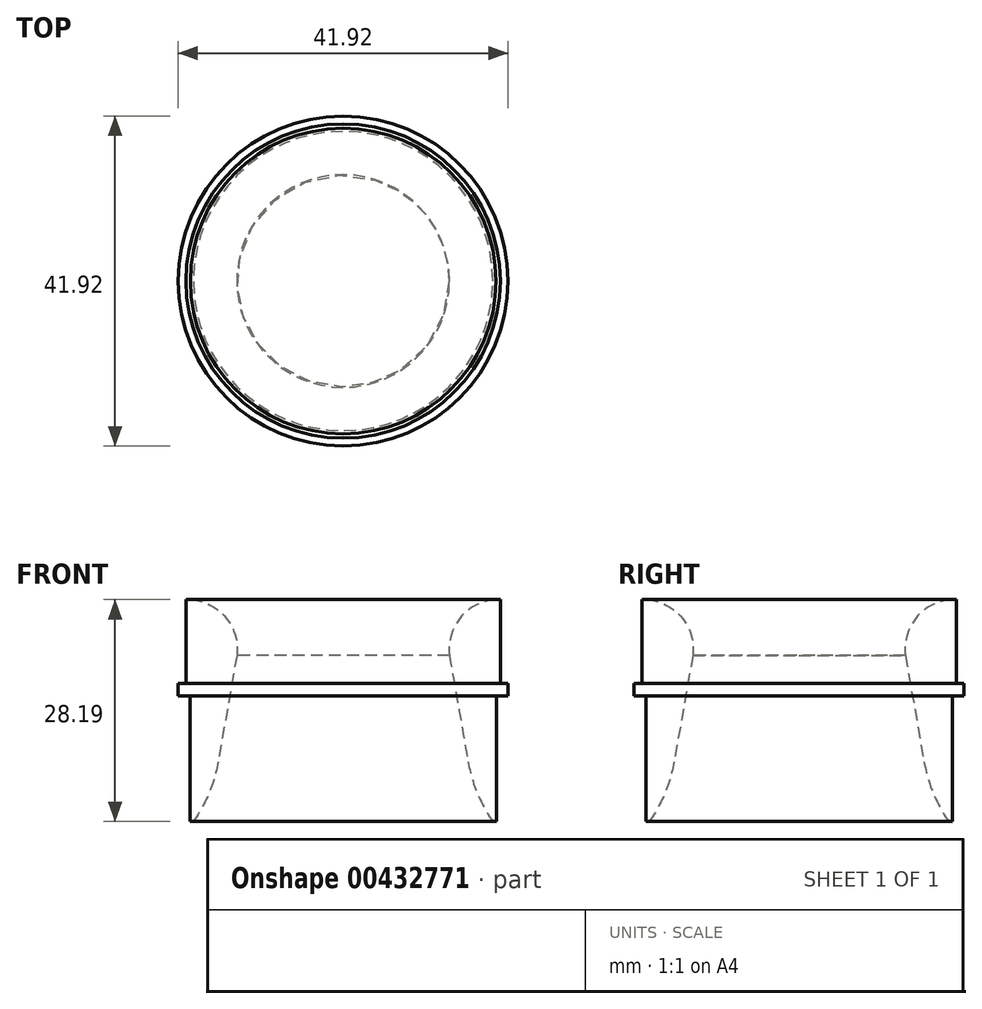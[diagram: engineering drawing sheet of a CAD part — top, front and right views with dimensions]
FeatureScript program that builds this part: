
annotation { "Feature Type Name" : "Feature", "Feature Type Description" : "" }
export const myFeature = defineFeature(function(context is Context, id is Id, definition is map)
    precondition{}
    {
        {
            var Q0;
            Q0=qCreatedBy(makeId("Front.planeOp"),FACE);
            var sketch = newSketch(context, id + "F0", { "sketchPlane" : qUnion([Q0])});
            skLineSegment(sketch, "E0", {"start": v(-20.96, 0.41) * mm, "end": v(-20.96, -1.16) * mm});
            skLineSegment(sketch, "E1", {"start": v(-20.96, -1.16) * mm, "end": v(-19.46, -1.16) * mm});
            skLineSegment(sketch, "E2", {"start": v(-19.46, -1.16) * mm, "end": v(-19.46, -17.11) * mm});
            skLineSegment(sketch, "E3", {"start": v(-19.46, -17.11) * mm, "end": v(-19.01, -17.11) * mm});
            skLineSegment(sketch, "E4", {"start": v(-13.5, 3.97) * mm, "end": v(-15.88, -9.53) * mm});
            skArc(sketch, "E5", {"start": v(-15.88, -9.53) * mm, "mid": v(-17.03, -13.5) * mm, "end": v(-19.01, -17.11) * mm});
            skLineSegment(sketch, "E6", {"start": v(0, 21.2) * mm, "end": v(0, 3.97) * mm});
            skLineSegment(sketch, "E7", {"start": v(-13.5, 3.97) * mm, "end": v(0, 3.97) * mm});
            skLineSegment(sketch, "E8", {"start": v(-19.96, 11.08) * mm, "end": v(-19.4, 11.08) * mm});
            skLineSegment(sketch, "E9", {"start": v(-19.96, 11.08) * mm, "end": v(-19.96, 0.41) * mm});
            skLineSegment(sketch, "E10", {"start": v(-19.96, 0.41) * mm, "end": v(-20.96, 0.41) * mm});
            skArc(sketch, "E11", {"start": v(-13.5, 3.97) * mm, "mid": v(-14.92, 8.8) * mm, "end": v(-19.4, 11.08) * mm});
            skPoint(sketch, "E12.start.orphan", {"position": v(0, 11.08) * mm});
            skPoint(sketch, "E13.trimOffspring.start.orphan", {"position": v(0, -17.11) * mm});
            skSolve(sketch);
        }
        {
            var Q0;
            {var subQ4=sQuery(id+"F0.wireOp",EDGE,"R1z6lWhH-c3eX-9CHA-9b9P-jS836zFYaLfb");Q0=makeQuery(id+"F0.imprint","IMPRINT",FACE,{"disambiguationData":[TD([[makeQuery(id+"F0.imprint","IMPRINT",EDGE,{"derivedFrom":subQ4}),1.0]])]});}
            var Q1;
            Q1=makeQuery(id+"F0.imprint","IMPRINT",FACE,{"disambiguationData":[TD([[makeQuery(id+"F0.imprint","IMPRINT",EDGE,{"derivedFrom":sQuery(id+"F0.wireOp",EDGE,"E0")}),1.0]])]});
            var Q2;
            Q2=sQuery(id+"F0.wireOp",EDGE,"E6");
            revolve(context, id + "F1", {"entities" : qUnion([Q0, Q1]), "axis" : qUnion([Q2]), "revolveType" : RevolveType.FULL});
        }
    });
